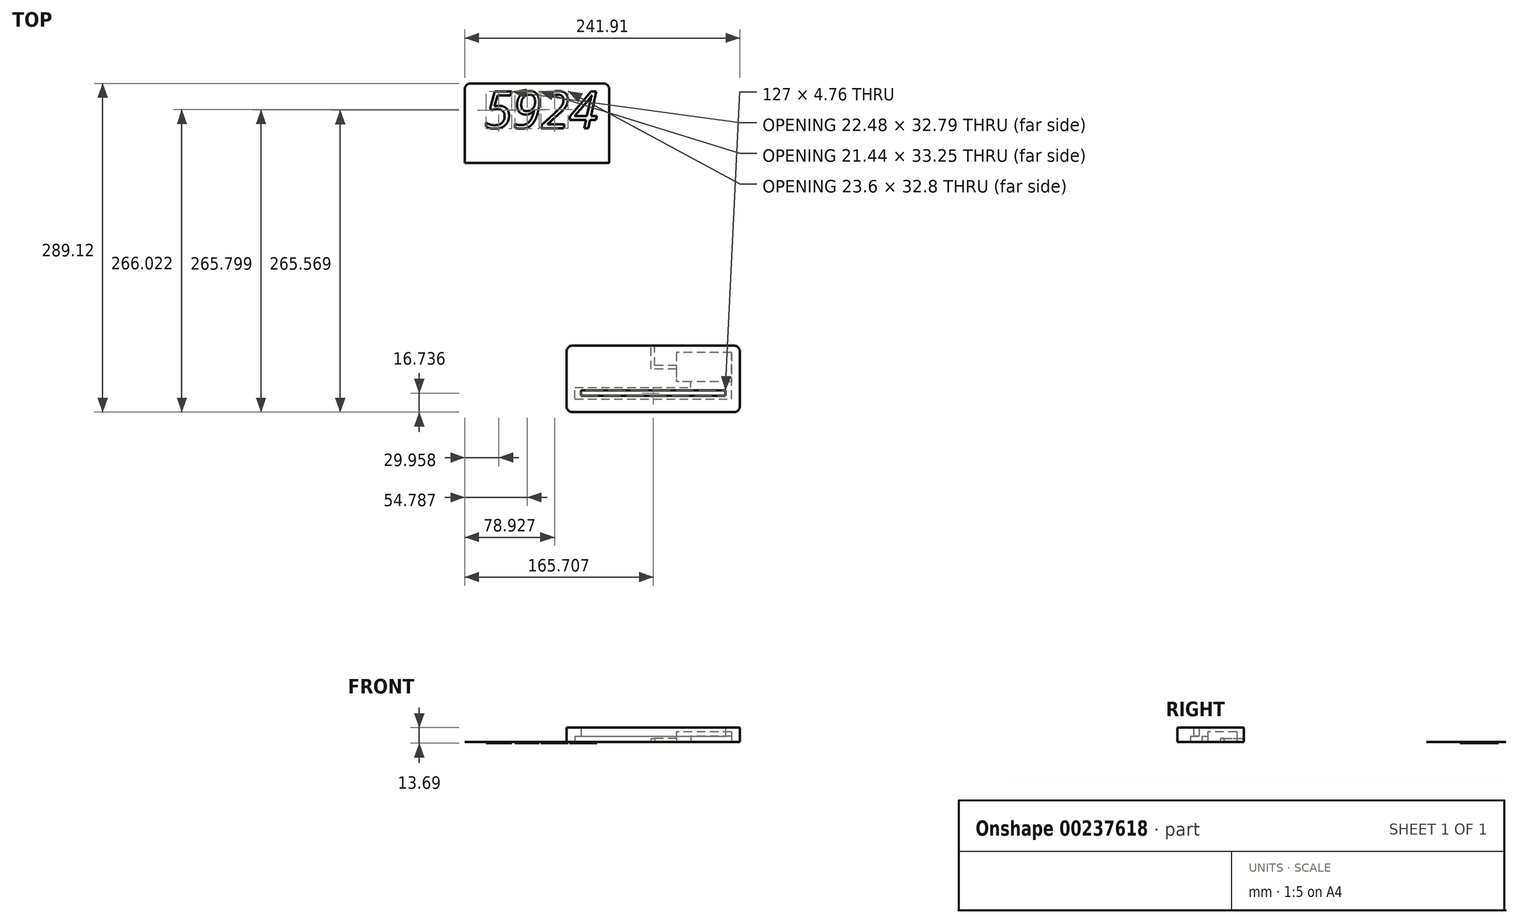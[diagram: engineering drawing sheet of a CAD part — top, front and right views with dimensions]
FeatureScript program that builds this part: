
annotation { "Feature Type Name" : "Feature", "Feature Type Description" : "" }
export const myFeature = defineFeature(function(context is Context, id is Id, definition is map)
    precondition{}
    {
        {
            assignVariable(context, id + "F0", {"name" : "led_thickness", "anyValue" : 5.08 * mm});
        }
        {
            assignVariable(context, id + "F1", {"name" : "base_thickness", "anyValue" : 12.7 * mm});
        }
        {
            assignVariable(context, id + "F2", {"name" : "acrylic_thickness", "anyValue" : 3 / 406.4 * mm});
        }
        {
            var Q0;
            Q0=qCreatedBy(makeId("Top.planeOp"),FACE);
            var sketch = newSketch(context, id + "F3", { "sketchPlane" : qUnion([Q0])});
            skLineSegment(sketch, "E0.bottom", {"start": v(-85.8, 47.77) * mm, "end": v(66.6, 47.77) * mm});
            skLineSegment(sketch, "E0.top", {"start": v(-85.8, -10.65) * mm, "end": v(66.6, -10.65) * mm});
            skLineSegment(sketch, "E0.left", {"start": v(-85.8, 47.77) * mm, "end": v(-85.8, -10.65) * mm});
            skLineSegment(sketch, "E0.right", {"start": v(66.6, 47.77) * mm, "end": v(66.6, -10.65) * mm});
            skLineSegment(sketch, "E1", {"start": v(-25.65, 6.09) * mm, "end": v(6.46, 6.09) * mm, "construction": true});
            skPoint(sketch, "E2", {"position": v(-9.6, 6.09) * mm});
            skPoint(sketch, "E3", {"position": v(-9.6, 47.77) * mm});
            skLineSegment(sketch, "E4.bottom", {"start": v(-73.1, 8.47) * mm, "end": v(53.9, 8.47) * mm});
            skLineSegment(sketch, "E4.top", {"start": v(-73.1, 3.7) * mm, "end": v(53.9, 3.7) * mm});
            skLineSegment(sketch, "E4.left", {"start": v(-73.1, 8.47) * mm, "end": v(-73.1, 3.7) * mm});
            skLineSegment(sketch, "E4.right", {"start": v(53.9, 8.47) * mm, "end": v(53.9, 3.7) * mm});
            skSolve(sketch);
        }
        {
            var Q0;
            Q0=makeQuery(id+"F3.imprint","IMPRINT",FACE,{"disambiguationData":[TD([[makeQuery(id+"F3.imprint","IMPRINT",EDGE,{"derivedFrom":sQuery(id+"F3.wireOp",EDGE,"E0.bottom")}),-1.0]])]});
            var Q1;
            {var subQ1=sQuery(id+"F3.wireOp",EDGE,"238ec220-7128-4f95-b01a-69b673e17785.0");var subQ6=sQuery(id+"F3.wireOp",EDGE,"238ec220-7128-4f95-b01a-69b673e17785.1");var subQ9=makeQuery(id+"F3.imprint","INTERSECT",VERTEX,{"derivedFrom":[subQ1,subQ6]});Q1=makeQuery(id+"F3.imprint","IMPRINT",FACE,{"disambiguationData":[TD([[makeQuery(id+"F3.imprint","IMPRINT",EDGE,{"disambiguationData":[TD([[subQ9,-1.0]])],"derivedFrom":subQ1}),-1.0]])]});}
            var Q2;
            {var subQ1=sQuery(id+"F3.wireOp",EDGE,"238ec220-7128-4f95-b01a-69b673e17785.1");var subQ7=sQuery(id+"F3.wireOp",EDGE,"238ec220-7128-4f95-b01a-69b673e17785.2");var subQ8=makeQuery(id+"F3.imprint","INTERSECT",VERTEX,{"derivedFrom":[subQ1,subQ7]});Q2=makeQuery(id+"F3.imprint","IMPRINT",FACE,{"disambiguationData":[TD([[makeQuery(id+"F3.imprint","IMPRINT",EDGE,{"disambiguationData":[TD([[subQ8,1.0]])],"derivedFrom":subQ1}),1.0]])]});}
            var Q3;
            {var subQ1=sQuery(id+"F3.wireOp",EDGE,"238ec220-7128-4f95-b01a-69b673e17785.0");var subQ5=sQuery(id+"F3.wireOp",EDGE,"238ec220-7128-4f95-b01a-69b673e17785.3");var subQ6=makeQuery(id+"F3.imprint","INTERSECT",VERTEX,{"derivedFrom":[subQ1,subQ5]});Q3=makeQuery(id+"F3.imprint","IMPRINT",FACE,{"disambiguationData":[TD([[makeQuery(id+"F3.imprint","IMPRINT",EDGE,{"disambiguationData":[TD([[subQ6,1.0]])],"derivedFrom":subQ1}),-1.0]])]});}
            var Q4;
            {var subQ1=sQuery(id+"F3.wireOp",EDGE,"238ec220-7128-4f95-b01a-69b673e17785.3");var subQ6=sQuery(id+"F3.wireOp",EDGE,"238ec220-7128-4f95-b01a-69b673e17785.2");var subQ9=makeQuery(id+"F3.imprint","INTERSECT",VERTEX,{"derivedFrom":[subQ6,subQ1]});Q4=makeQuery(id+"F3.imprint","IMPRINT",FACE,{"disambiguationData":[TD([[makeQuery(id+"F3.imprint","IMPRINT",EDGE,{"disambiguationData":[TD([[subQ9,1.0]])],"derivedFrom":subQ6}),1.0]])]});}
            var Q5;
            {var subQ0=sQuery(id+"F3.wireOp",EDGE,"KGYifipC-A0Ze-Ky2Y-kKE0-6M0a031VCRZl");var subQ1=sQuery(id+"F3.wireOp",EDGE,"gFtBQQrP-z6kP-i91m-ujdm-oMehcq1cFs6k");var subQ2=makeQuery(id+"F3.imprint","INTERSECT",VERTEX,{"derivedFrom":[subQ1,subQ0]});Q5=makeQuery(id+"F3.imprint","IMPRINT",FACE,{"disambiguationData":[TD([[makeQuery(id+"F3.imprint","IMPRINT",EDGE,{"disambiguationData":[TD([[subQ2,-1.0]])],"derivedFrom":subQ1}),1.0]])]});}
            extrude(context, id + "F4", {"entities" : qUnion([Q0, Q1, Q2, Q3, Q4, Q5]), "depth" : getVariable(context, 'base_thickness')});
        }
        {
            var Q0;
            Q0=makeQuery(id+"F4.opExtrude","CAP_FACE",FACE,{"disambiguationData":[OSD([sQuery(id+"F3.wireOp",EDGE,"E0.bottom"),sQuery(id+"F3.wireOp",EDGE,"E0.top"),sQuery(id+"F3.wireOp",EDGE,"E0.left"),sQuery(id+"F3.wireOp",EDGE,"E0.right"),sQuery(id+"F3.wireOp",EDGE,"E4.bottom"),sQuery(id+"F3.wireOp",EDGE,"E4.top"),sQuery(id+"F3.wireOp",EDGE,"E4.left"),sQuery(id+"F3.wireOp",EDGE,"E4.right")])],"isStart":true});
            var sketch = newSketch(context, id + "F5", { "sketchPlane" : qUnion([Q0])});
            skLineSegment(sketch, "E5.0", {"start": v(-73.1, -3.7) * mm, "end": v(53.9, -3.7) * mm});
            skLineSegment(sketch, "E6.0", {"start": v(-73.1, -8.47) * mm, "end": v(53.9, -8.47) * mm});
            skPoint(sketch, "E7.0", {"position": v(-73.1, -6.09) * mm});
            skPoint(sketch, "E8.0", {"position": v(53.9, -6.09) * mm});
            skLineSegment(sketch, "E9.bottom", {"start": v(-78.43, -1) * mm, "end": v(59.24, -1) * mm});
            skLineSegment(sketch, "E9.top", {"start": v(-78.43, -11.17) * mm, "end": v(59.24, -11.17) * mm});
            skLineSegment(sketch, "E9.left", {"start": v(-78.43, -1) * mm, "end": v(-78.43, -11.17) * mm});
            skLineSegment(sketch, "E9.right", {"start": v(59.24, -1) * mm, "end": v(59.24, -11.17) * mm});
            skPoint(sketch, "E9.middle", {"position": v(-9.6, -6.09) * mm});
            skPoint(sketch, "E9.middle.positionSnap0", {"position": v(-9.6, -3.7) * mm});
            skPoint(sketch, "E9.centerSnap0", {"position": v(-9.6, -3.7) * mm});
            skPoint(sketch, "E10.middle", {"position": v(35.04, -29) * mm});
            skLineSegment(sketch, "E11.bottom", {"start": v(59.24, -41.75) * mm, "end": v(10.84, -41.75) * mm});
            skLineSegment(sketch, "E11.top", {"start": v(59.24, -16.25) * mm, "end": v(10.84, -16.25) * mm});
            skLineSegment(sketch, "E11.left", {"start": v(59.24, -41.75) * mm, "end": v(59.24, -16.25) * mm});
            skLineSegment(sketch, "E11.right", {"start": v(10.84, -41.75) * mm, "end": v(10.84, -16.25) * mm});
            skLineSegment(sketch, "E12", {"start": v(23.55, -11.17) * mm, "end": v(23.55, -16.25) * mm});
            skLineSegment(sketch, "E13", {"start": v(59.24, -11.17) * mm, "end": v(59.24, -16.25) * mm});
            skLineSegment(sketch, "E14", {"start": v(10.84, -27.17) * mm, "end": v(-11.58, -27.17) * mm});
            skLineSegment(sketch, "E15", {"start": v(-11.58, -27.17) * mm, "end": v(-11.58, -47.77) * mm});
            skLineSegment(sketch, "E16", {"start": v(10.84, -30.34) * mm, "end": v(-8.4, -30.34) * mm});
            skLineSegment(sketch, "E17", {"start": v(-8.4, -30.34) * mm, "end": v(-8.4, -47.77) * mm});
            skLineSegment(sketch, "E18", {"start": v(-11.58, -47.77) * mm, "end": v(-8.4, -47.77) * mm});
            skLineSegment(sketch, "E19", {"start": v(-8.4, -42.54) * mm, "end": v(-11.58, -42.54) * mm, "construction": true});
            skLineSegment(sketch, "E20", {"start": v(4.48, -27.17) * mm, "end": v(4.48, -30.34) * mm, "construction": true});
            skSolve(sketch);
        }
        {
            var Q0;
            Q0=makeQuery(id+"F5.imprint","IMPRINT",FACE,{"disambiguationData":[TD([[makeQuery(id+"F5.imprint","IMPRINT",EDGE,{"derivedFrom":sQuery(id+"F5.wireOp",EDGE,"E5.0")}),1.0]])]});
            var Q1;
            {var subQ2=sQuery(id+"F5.wireOp",EDGE,"E12");Q1=makeQuery(id+"F5.imprint","IMPRINT",FACE,{"disambiguationData":[TD([[makeQuery(id+"F5.imprint","IMPRINT",EDGE,{"derivedFrom":subQ2}),1.0]])]});}
            extrude(context, id + "F6", {"entities" : qUnion([Q0, Q1]), "operationType" : NewBodyOperationType.REMOVE, "oppositeDirection" : true, "depth" : getVariable(context, 'led_thickness')});
        }
        {
            var Q0;
            Q0=makeQuery(id+"F4.opExtrude","SWEPT_EDGE",EDGE,{"disambiguationData":[OSD([sQuery(id+"F3.wireOp",EDGE,"E0.top"),sQuery(id+"F3.wireOp",EDGE,"E0.left")])]});
            var Q1;
            Q1=makeQuery(id+"F4.opExtrude","SWEPT_EDGE",EDGE,{"disambiguationData":[OSD([sQuery(id+"F3.wireOp",EDGE,"E0.top"),sQuery(id+"F3.wireOp",EDGE,"E0.right")])]});
            var Q2;
            Q2=makeQuery(id+"F4.opExtrude","SWEPT_EDGE",EDGE,{"disambiguationData":[OSD([sQuery(id+"F3.wireOp",EDGE,"E0.bottom"),sQuery(id+"F3.wireOp",EDGE,"E0.right")])]});
            var Q3;
            Q3=makeQuery(id+"F4.opExtrude","SWEPT_EDGE",EDGE,{"disambiguationData":[OSD([sQuery(id+"F3.wireOp",EDGE,"E0.bottom"),sQuery(id+"F3.wireOp",EDGE,"E0.left")])]});
            fillet(context, id + "F7", {"entities" : qUnion([Q0, Q1, Q2, Q3]), "radius" : 5.08 * mm, "tangentPropagation" : true, "allowEdgeOverflow" : false});
        }
        {
            var Q0;
            Q0=makeQuery(id+"F5.imprint","IMPRINT",FACE,{"disambiguationData":[TD([[makeQuery(id+"F5.imprint","IMPRINT",EDGE,{"derivedFrom":sQuery(id+"F5.wireOp",EDGE,"E11.bottom")}),-1.0]])]});
            extrude(context, id + "F8", {"entities" : qUnion([Q0]), "operationType" : NewBodyOperationType.REMOVE, "oppositeDirection" : true, "depth" : 8.9 * mm});
        }
        {
            var Q0;
            Q0=qCreatedBy(makeId("Top.planeOp"),FACE);
            var sketch = newSketch(context, id + "F9", { "sketchPlane" : qUnion([Q0])});
            skLineSegment(sketch, "E21.bottom", {"start": v(-48.3, 208.62) * mm, "end": v(-175.3, 208.62) * mm});
            skLineSegment(sketch, "E21.top", {"start": v(-48.3, 278.47) * mm, "end": v(-175.3, 278.47) * mm});
            skLineSegment(sketch, "E21.left", {"start": v(-48.3, 208.62) * mm, "end": v(-48.3, 278.47) * mm});
            skLineSegment(sketch, "E21.right", {"start": v(-175.3, 208.62) * mm, "end": v(-175.3, 278.47) * mm});
            skPoint(sketch, "E21.middle", {"position": v(-111.8, 243.54) * mm});
            skText(sketch, "E22", { "text": "5924", "fontName": "OpenSans-Italic.ttf"});
            const initialGuessF9  = {"E22": [-0.15835, 0.23897, 1, 0, 0.03262]};
            skSetInitialGuess(sketch, initialGuessF9);
            skSolve(sketch);
        }
        {
            var Q0;
            Q0 = qSketchRegion(id + "F9", true);
            var Q1;
            Q1=makeQuery(id+"F9.imprint","IMPRINT",FACE,{"disambiguationData":[TD([[makeQuery(id+"F9.imprint","IMPRINT",EDGE,{"derivedFrom":sQuery(id+"F9.wireOp",EDGE,"E22.sketch_text.stroke-40")}),1.0]])]});
            var Q2;
            Q2=makeQuery(id+"F9.imprint","IMPRINT",FACE,{"disambiguationData":[TD([[makeQuery(id+"F9.imprint","IMPRINT",EDGE,{"derivedFrom":sQuery(id+"F9.wireOp",EDGE,"E22.sketch_text.stroke-83")}),1.0]])]});
            extrude(context, id + "F10", {"entities" : qUnion([Q0, Q1, Q2]), "depth" : getVariable(context, 'acrylic_thickness')});
        }
        {
            var Q0;
            Q0=makeQuery(id+"F9.imprint","IMPRINT",FACE,{"disambiguationData":[TD([[makeQuery(id+"F9.imprint","IMPRINT",EDGE,{"derivedFrom":sQuery(id+"F9.wireOp",EDGE,"E22.sketch_text.stroke-0")}),-1.0]])]});
            var Q1;
            Q1=makeQuery(id+"F9.imprint","IMPRINT",FACE,{"disambiguationData":[TD([[makeQuery(id+"F9.imprint","IMPRINT",EDGE,{"derivedFrom":sQuery(id+"F9.wireOp",EDGE,"E22.sketch_text.stroke-21")}),-1.0]])]});
            var Q2;
            Q2=makeQuery(id+"F9.imprint","IMPRINT",FACE,{"disambiguationData":[TD([[makeQuery(id+"F9.imprint","IMPRINT",EDGE,{"derivedFrom":sQuery(id+"F9.wireOp",EDGE,"E22.sketch_text.stroke-50")}),-1.0]])]});
            var Q3;
            Q3=makeQuery(id+"F9.imprint","IMPRINT",FACE,{"disambiguationData":[TD([[makeQuery(id+"F9.imprint","IMPRINT",EDGE,{"derivedFrom":sQuery(id+"F9.wireOp",EDGE,"E22.sketch_text.stroke-72")}),-1.0]])]});
            extrude(context, id + "F11", {"entities" : qUnion([Q0, Q1, Q2, Q3]), "operationType" : NewBodyOperationType.ADD, "depth" : getVariable(context, 'acrylic_thickness') - 1 * mm});
        }
        {
            var Q0;
            Q0=makeQuery(id+"F10.opExtrude","SWEPT_EDGE",EDGE,{"disambiguationData":[OSD([sQuery(id+"F9.wireOp",EDGE,"E21.top"),sQuery(id+"F9.wireOp",EDGE,"E21.right")])]});
            var Q1;
            Q1=makeQuery(id+"F10.opExtrude","SWEPT_EDGE",EDGE,{"disambiguationData":[OSD([sQuery(id+"F9.wireOp",EDGE,"E21.top"),sQuery(id+"F9.wireOp",EDGE,"E21.left")])]});
            fillet(context, id + "F12", {"entities" : qUnion([Q0, Q1]), "radius" : 5.08 * mm, "tangentPropagation" : true, "allowEdgeOverflow" : false});
        }
        {
            var Q0;
            {var subQ1=sQuery(id+"F5.wireOp",EDGE,"E14");Q0=makeQuery(id+"F5.imprint","IMPRINT",FACE,{"disambiguationData":[TD([[makeQuery(id+"F5.imprint","IMPRINT",EDGE,{"derivedFrom":subQ1}),1.0]])]});}
            extrude(context, id + "F13", {"entities" : qUnion([Q0]), "operationType" : NewBodyOperationType.REMOVE, "oppositeDirection" : true, "depth" : 3.3 * mm});
        }
    });
